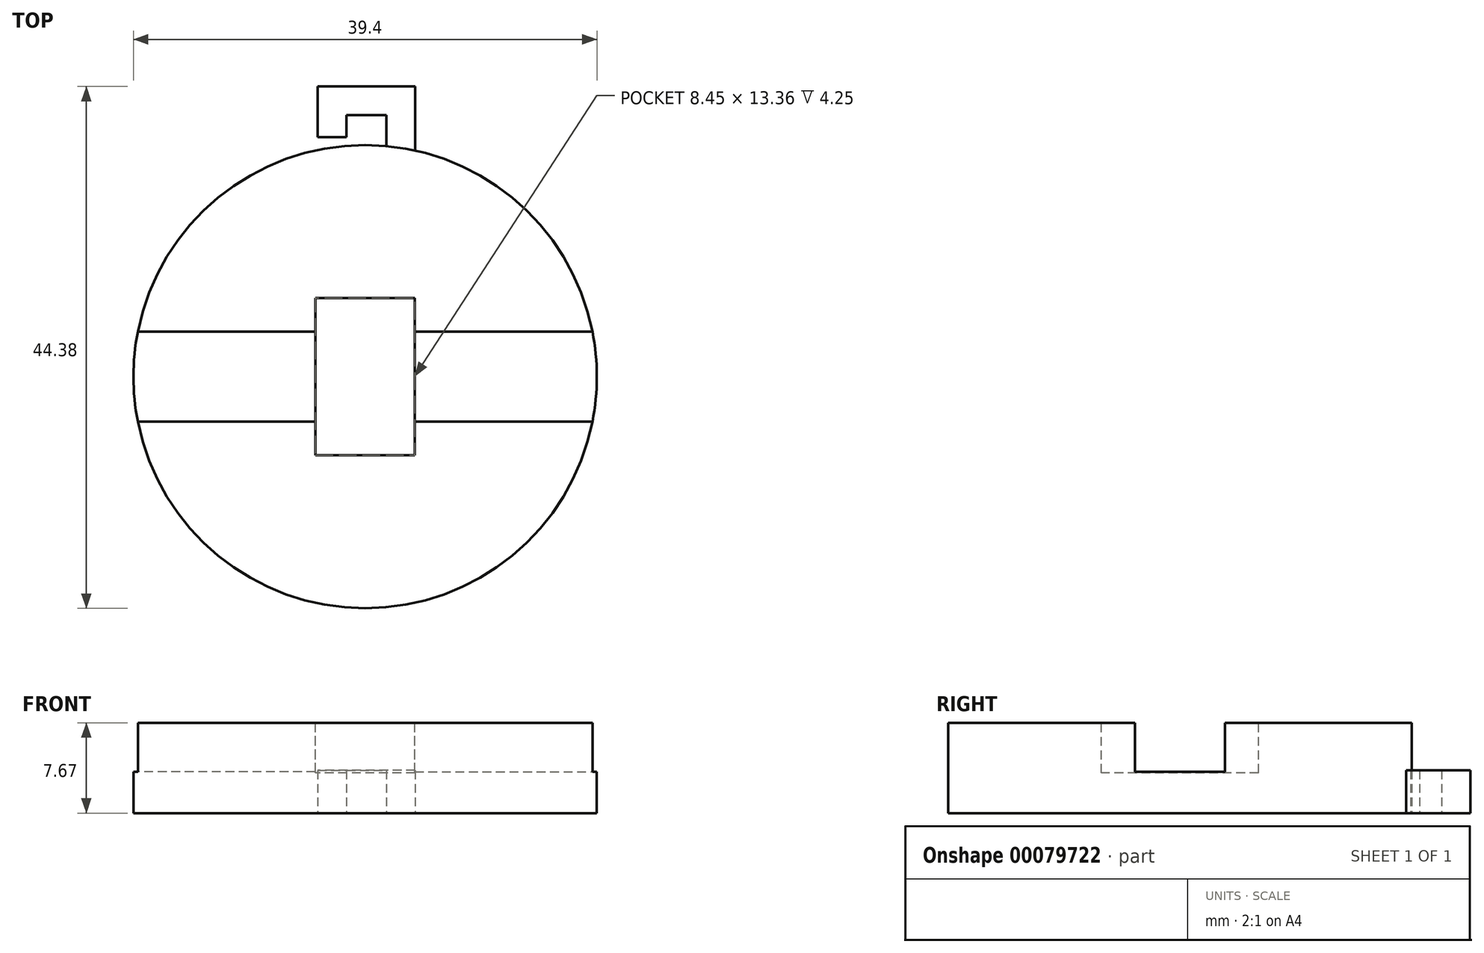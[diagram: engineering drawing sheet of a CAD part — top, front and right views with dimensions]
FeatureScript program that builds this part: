
annotation { "Feature Type Name" : "Feature", "Feature Type Description" : "" }
export const myFeature = defineFeature(function(context is Context, id is Id, definition is map)
    precondition{}
    {
        {
            var Q0;
            Q0=qCreatedBy(makeId("Top.planeOp"),FACE);
            var sketch = newSketch(context, id + "F0", { "sketchPlane" : qUnion([Q0])});
            skCircle(sketch, "E0", {"center": v(0, 0) * mm, "radius": 19.7 * mm});
            skLineSegment(sketch, "E1", {"start": v(4.25, 19.23) * mm, "end": v(4.25, 24.68) * mm});
            skLineSegment(sketch, "E2", {"start": v(4.25, 24.68) * mm, "end": v(-4.03, 24.68) * mm});
            skLineSegment(sketch, "E3", {"start": v(-4.03, 24.68) * mm, "end": v(-4.03, 20.38) * mm});
            skLineSegment(sketch, "E4", {"start": v(-4.03, 20.38) * mm, "end": v(-1.58, 20.38) * mm});
            skLineSegment(sketch, "E5", {"start": v(-1.58, 20.38) * mm, "end": v(-1.58, 22.23) * mm});
            skLineSegment(sketch, "E6", {"start": v(-1.58, 22.23) * mm, "end": v(1.8, 22.23) * mm});
            skLineSegment(sketch, "E7", {"start": v(1.8, 22.23) * mm, "end": v(1.8, 19.61) * mm});
            skSolve(sketch);
        }
        {
            var Q0;
            {var subQ0=sQuery(id+"F0.wireOp",EDGE,"E0");var subQ1=makeQuery(id+"F0.imprint","INTERSECT",VERTEX,{"derivedFrom":[subQ0,sQuery(id+"F0.wireOp",EDGE,"E1")]});Q0=makeQuery(id+"F0.imprint","IMPRINT",FACE,{"disambiguationData":[TD([[makeQuery(id+"F0.imprint","IMPRINT",EDGE,{"disambiguationData":[TD([[subQ1,-1.0]])],"derivedFrom":subQ0}),1.0]])]});}
            extrude(context, id + "F1", {"entities" : qUnion([Q0]), "depth" : 7.67 * mm});
        }
        {
            var Q0;
            {var subQ0=sQuery(id+"F0.wireOp",EDGE,"E1");Q0=makeQuery(id+"F0.imprint","IMPRINT",FACE,{"disambiguationData":[TD([[makeQuery(id+"F0.imprint","IMPRINT",EDGE,{"derivedFrom":subQ0}),1.0]])]});}
            extrude(context, id + "F2", {"entities" : qUnion([Q0]), "operationType" : NewBodyOperationType.ADD, "depth" : 3.63 * mm});
        }
        {
            var Q0;
            Q0=makeQuery(id+"F1.opExtrude","CAP_FACE",FACE,{"disambiguationData":[OSD([sQuery(id+"F0.wireOp",EDGE,"E0")])],"isStart":false});
            var sketch = newSketch(context, id + "F3", { "sketchPlane" : qUnion([Q0])});
            skLineSegment(sketch, "E8.bottom", {"start": v(4.23, 6.68) * mm, "end": v(-4.23, 6.68) * mm});
            skLineSegment(sketch, "E8.top", {"start": v(4.23, -6.68) * mm, "end": v(-4.23, -6.68) * mm});
            skLineSegment(sketch, "E8.left", {"start": v(4.23, 6.68) * mm, "end": v(4.23, -6.68) * mm});
            skLineSegment(sketch, "E8.right", {"start": v(-4.23, 6.68) * mm, "end": v(-4.23, -6.68) * mm});
            skPoint(sketch, "E8.middle", {"position": v(0, 0) * mm});
            skLineSegment(sketch, "E9", {"start": v(4.23, 3.83) * mm, "end": v(19.32, 3.83) * mm});
            skLineSegment(sketch, "E10", {"start": v(4.23, -3.83) * mm, "end": v(19.32, -3.83) * mm});
            skLineSegment(sketch, "E11", {"start": v(-4.23, 3.83) * mm, "end": v(-19.32, 3.83) * mm});
            skLineSegment(sketch, "E12", {"start": v(-4.23, -3.83) * mm, "end": v(-19.32, -3.83) * mm});
            skSolve(sketch);
        }
        {
            var Q0;
            {var subQ3=sQuery(id+"F3.wireOp",EDGE,"E8.bottom");Q0=makeQuery(id+"F3.imprint","IMPRINT",FACE,{"disambiguationData":[TD([[makeQuery(id+"F3.imprint","IMPRINT",EDGE,{"derivedFrom":subQ3}),1.0]])]});}
            extrude(context, id + "F4", {"entities" : qUnion([Q0]), "operationType" : NewBodyOperationType.REMOVE, "oppositeDirection" : true, "depth" : 4.25 * mm});
        }
        {
            var Q0;
            {var subQ0=sQuery(id+"F3.wireOp",EDGE,"E11");Q0=makeQuery(id+"F3.imprint","IMPRINT",FACE,{"disambiguationData":[TD([[makeQuery(id+"F3.imprint","IMPRINT",EDGE,{"derivedFrom":subQ0}),1.0]])]});}
            var Q1;
            {var subQ0=sQuery(id+"F3.wireOp",EDGE,"E9");Q1=makeQuery(id+"F3.imprint","IMPRINT",FACE,{"disambiguationData":[TD([[makeQuery(id+"F3.imprint","IMPRINT",EDGE,{"derivedFrom":subQ0}),-1.0]])]});}
            extrude(context, id + "F5", {"entities" : qUnion([Q0, Q1]), "operationType" : NewBodyOperationType.REMOVE, "oppositeDirection" : true, "depth" : 4.15 * mm});
        }
    });
